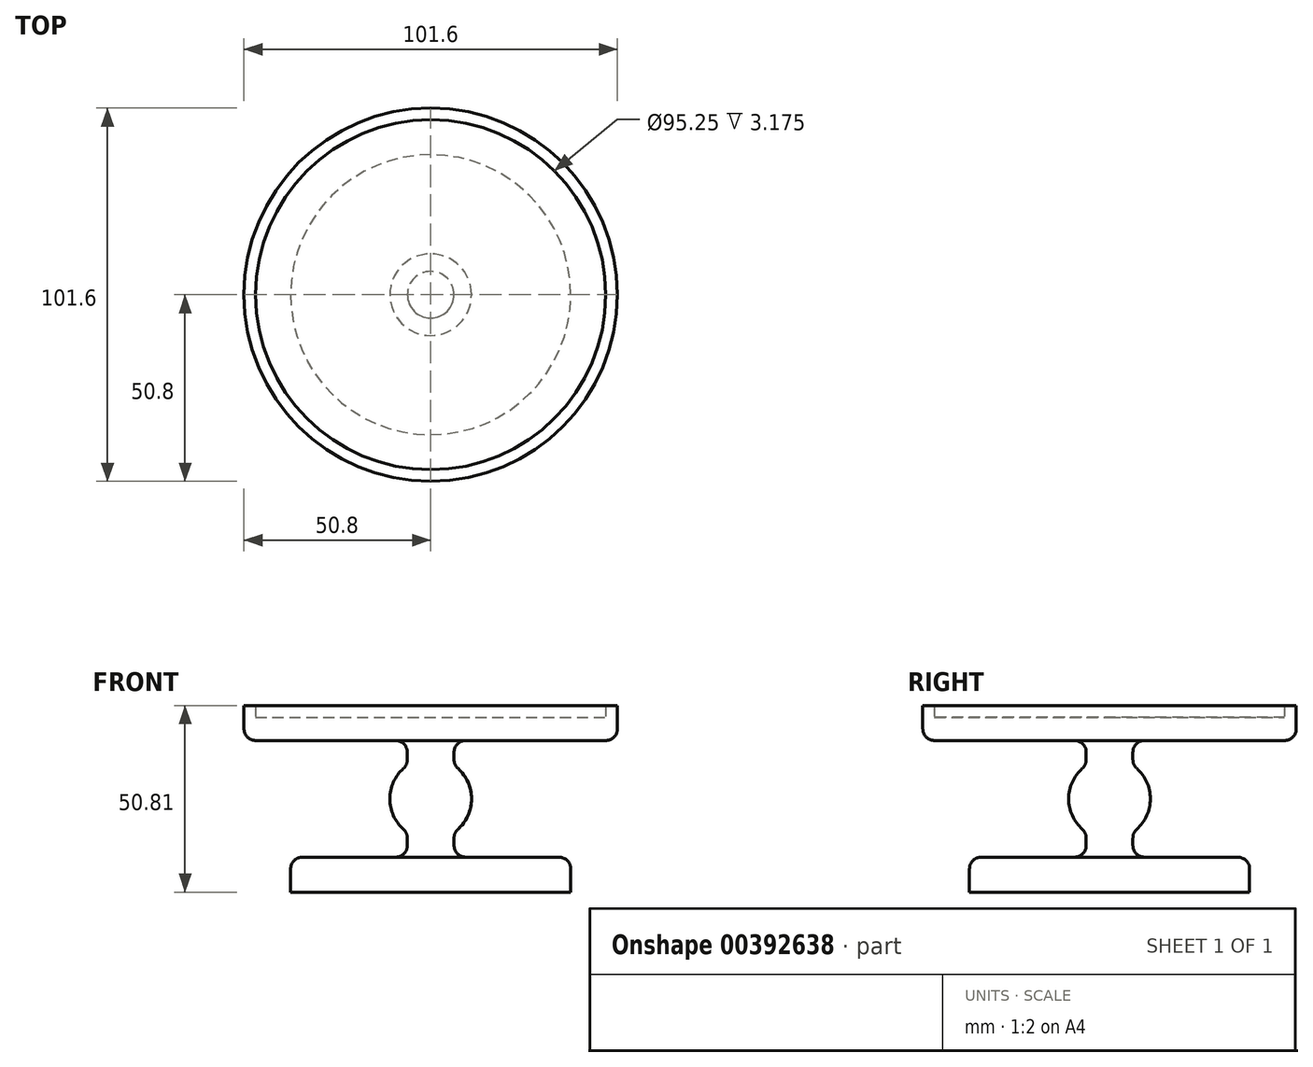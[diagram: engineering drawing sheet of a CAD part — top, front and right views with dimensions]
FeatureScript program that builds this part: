
annotation { "Feature Type Name" : "Feature", "Feature Type Description" : "" }
export const myFeature = defineFeature(function(context is Context, id is Id, definition is map)
    precondition{}
    {
        {
            var Q0;
            Q0=qCreatedBy(makeId("Front.planeOp"),FACE);
            var sketch = newSketch(context, id + "F0", { "sketchPlane" : qUnion([Q0])});
            skLineSegment(sketch, "E0", {"start": v(0, 0) * mm, "end": v(0, 39.38) * mm, "construction": true});
            skLineSegment(sketch, "E1.bottom", {"start": v(0, 0) * mm, "end": v(50.8, 0) * mm});
            skLineSegment(sketch, "E1.top", {"start": v(0, 9.52) * mm, "end": v(50.8, 9.53) * mm});
            skLineSegment(sketch, "E1.left", {"start": v(0, 0) * mm, "end": v(0, 9.52) * mm});
            skLineSegment(sketch, "E1.right", {"start": v(50.8, 0) * mm, "end": v(50.8, 9.53) * mm});
            skLineSegment(sketch, "E2.bottom", {"start": v(0, 0) * mm, "end": v(6.35, 0) * mm});
            skLineSegment(sketch, "E2.top", {"start": v(0, -31.75) * mm, "end": v(6.35, -31.75) * mm});
            skLineSegment(sketch, "E2.left", {"start": v(0, 0) * mm, "end": v(0, -31.75) * mm});
            skLineSegment(sketch, "E2.right", {"start": v(6.35, 0) * mm, "end": v(6.35, -31.75) * mm});
            skLineSegment(sketch, "E3.bottom", {"start": v(0, -31.75) * mm, "end": v(38.1, -31.75) * mm});
            skLineSegment(sketch, "E3.top", {"start": v(0, -41.28) * mm, "end": v(38.1, -41.27) * mm});
            skLineSegment(sketch, "E3.left", {"start": v(0, -31.75) * mm, "end": v(0, -41.28) * mm});
            skLineSegment(sketch, "E3.right", {"start": v(38.1, -31.75) * mm, "end": v(38.1, -41.27) * mm});
            skCircle(sketch, "E4", {"center": v(0, -15.88) * mm, "radius": 11.11 * mm});
            skLineSegment(sketch, "E5.bottom", {"start": v(0, 9.52) * mm, "end": v(47.63, 9.52) * mm});
            skLineSegment(sketch, "E5.top", {"start": v(0, 6.35) * mm, "end": v(47.63, 6.35) * mm});
            skLineSegment(sketch, "E5.left", {"start": v(0, 9.52) * mm, "end": v(0, 6.35) * mm});
            skLineSegment(sketch, "E5.right", {"start": v(47.63, 9.53) * mm, "end": v(47.63, 6.35) * mm});
            skSolve(sketch);
        }
        {
            var Q0;
            Q0=makeQuery(id+"F0.imprint","IMPRINT",FACE,{"disambiguationData":[TD([[makeQuery(id+"F0.imprint","IMPRINT",EDGE,{"derivedFrom":sQuery(id+"F0.wireOp",EDGE,"E1.bottom")}),1.0]])]});
            var Q1;
            {var subQ0=sQuery(id+"F0.wireOp",EDGE,"U21skX3g-FfZw-KlHb-enD1-Xzze7m9jfw0C");var subQ1=sQuery(id+"F0.wireOp",EDGE,"E2.right");var subQ2=makeQuery(id+"F0.imprint","INTERSECT",VERTEX,{"disambiguationData":[OD(0.0)],"derivedFrom":[subQ1,subQ0]});Q1=makeQuery(id+"F0.imprint","IMPRINT",FACE,{"disambiguationData":[TD([[makeQuery(id+"F0.imprint","IMPRINT",EDGE,{"disambiguationData":[TD([[subQ2,-1.0]])],"derivedFrom":subQ1}),1.0]])]});}
            var Q2;
            Q2=makeQuery(id+"F0.imprint","IMPRINT",FACE,{"disambiguationData":[TD([[makeQuery(id+"F0.imprint","IMPRINT",EDGE,{"derivedFrom":sQuery(id+"F0.wireOp",EDGE,"E3.top")}),1.0]])]});
            var Q3;
            {var subQ0=sQuery(id+"F0.wireOp",EDGE,"E2.bottom");Q3=makeQuery(id+"F0.imprint","IMPRINT",FACE,{"disambiguationData":[TD([[makeQuery(id+"F0.imprint","IMPRINT",EDGE,{"derivedFrom":subQ0}),-1.0]])]});}
            var Q4;
            {var subQ0=sQuery(id+"F0.wireOp",EDGE,"E3.bottom");var subQ1=sQuery(id+"F0.wireOp",EDGE,"E2.right");var subQ2=makeQuery(id+"F0.imprint","INTERSECT",VERTEX,{"derivedFrom":[subQ1,subQ0]});Q4=makeQuery(id+"F0.imprint","IMPRINT",FACE,{"disambiguationData":[TD([[makeQuery(id+"F0.imprint","IMPRINT",EDGE,{"disambiguationData":[TD([[subQ2,1.0]])],"derivedFrom":subQ1}),-1.0]])]});}
            var Q5;
            {var subQ0=sQuery(id+"F0.wireOp",EDGE,"E2.left");Q5=makeQuery(id+"F0.imprint","IMPRINT",FACE,{"disambiguationData":[TD([[makeQuery(id+"F0.imprint","IMPRINT",EDGE,{"derivedFrom":subQ0}),1.0]])]});}
            var Q6;
            {var subQ0=sQuery(id+"F0.wireOp",EDGE,"E4");var subQ1=sQuery(id+"F0.wireOp",EDGE,"E2.right");var subQ2=makeQuery(id+"F0.imprint","INTERSECT",VERTEX,{"disambiguationData":[OD(0.0)],"derivedFrom":[subQ1,subQ0]});Q6=makeQuery(id+"F0.imprint","IMPRINT",FACE,{"disambiguationData":[TD([[makeQuery(id+"F0.imprint","IMPRINT",EDGE,{"disambiguationData":[TD([[subQ2,-1.0]])],"derivedFrom":subQ1}),1.0]])]});}
            var Q7;
            Q7=sQuery(id+"F0.wireOp",EDGE,"E0");
            revolve(context, id + "F1", {"entities" : qUnion([Q0, Q1, Q2, Q3, Q4, Q5, Q6]), "axis" : qUnion([Q7]), "revolveType" : RevolveType.FULL});
        }
        {
            var Q0;
            Q0=makeQuery(id+"F1.opRevolve","SWEPT_EDGE",EDGE,{"disambiguationData":[OSD([sQuery(id+"F0.wireOp",EDGE,"E1.bottom"),sQuery(id+"F0.wireOp",EDGE,"E2.bottom"),sQuery(id+"F0.wireOp",EDGE,"E2.right")])]});
            var Q1;
            {var subQ0=sQuery(id+"F0.wireOp",EDGE,"E4");var subQ1=sQuery(id+"F0.wireOp",EDGE,"E2.right");Q1=makeQuery(id+"F1.opRevolve","SWEPT_EDGE",EDGE,{"disambiguationData":[OSD([subQ1,subQ0]),TDD([makeQuery(id+"F0.imprint","INTERSECT",VERTEX,{"disambiguationData":[OD(0.0)],"derivedFrom":[subQ1,subQ0]})])]});}
            var Q2;
            {var subQ0=sQuery(id+"F0.wireOp",EDGE,"E4");var subQ1=sQuery(id+"F0.wireOp",EDGE,"E2.right");Q2=makeQuery(id+"F1.opRevolve","SWEPT_EDGE",EDGE,{"disambiguationData":[OSD([subQ1,subQ0]),TDD([makeQuery(id+"F0.imprint","INTERSECT",VERTEX,{"disambiguationData":[OD(1.0)],"derivedFrom":[subQ1,subQ0]})])]});}
            var Q3;
            Q3=makeQuery(id+"F1.opRevolve","SWEPT_EDGE",EDGE,{"disambiguationData":[OSD([sQuery(id+"F0.wireOp",EDGE,"E2.right"),sQuery(id+"F0.wireOp",EDGE,"E3.bottom")])]});
            var Q4;
            Q4=makeQuery(id+"F1.opRevolve","SWEPT_EDGE",EDGE,{"disambiguationData":[OSD([sQuery(id+"F0.wireOp",EDGE,"E1.bottom"),sQuery(id+"F0.wireOp",EDGE,"E1.right")])]});
            var Q5;
            Q5=makeQuery(id+"F1.opRevolve","SWEPT_EDGE",EDGE,{"disambiguationData":[OSD([sQuery(id+"F0.wireOp",EDGE,"E3.bottom"),sQuery(id+"F0.wireOp",EDGE,"E3.right")])]});
            fillet(context, id + "F2", {"entities" : qUnion([Q0, Q1, Q2, Q3, Q4, Q5]), "radius" : 3.17 * mm, "tangentPropagation" : true, "allowEdgeOverflow" : false});
        }
    });
